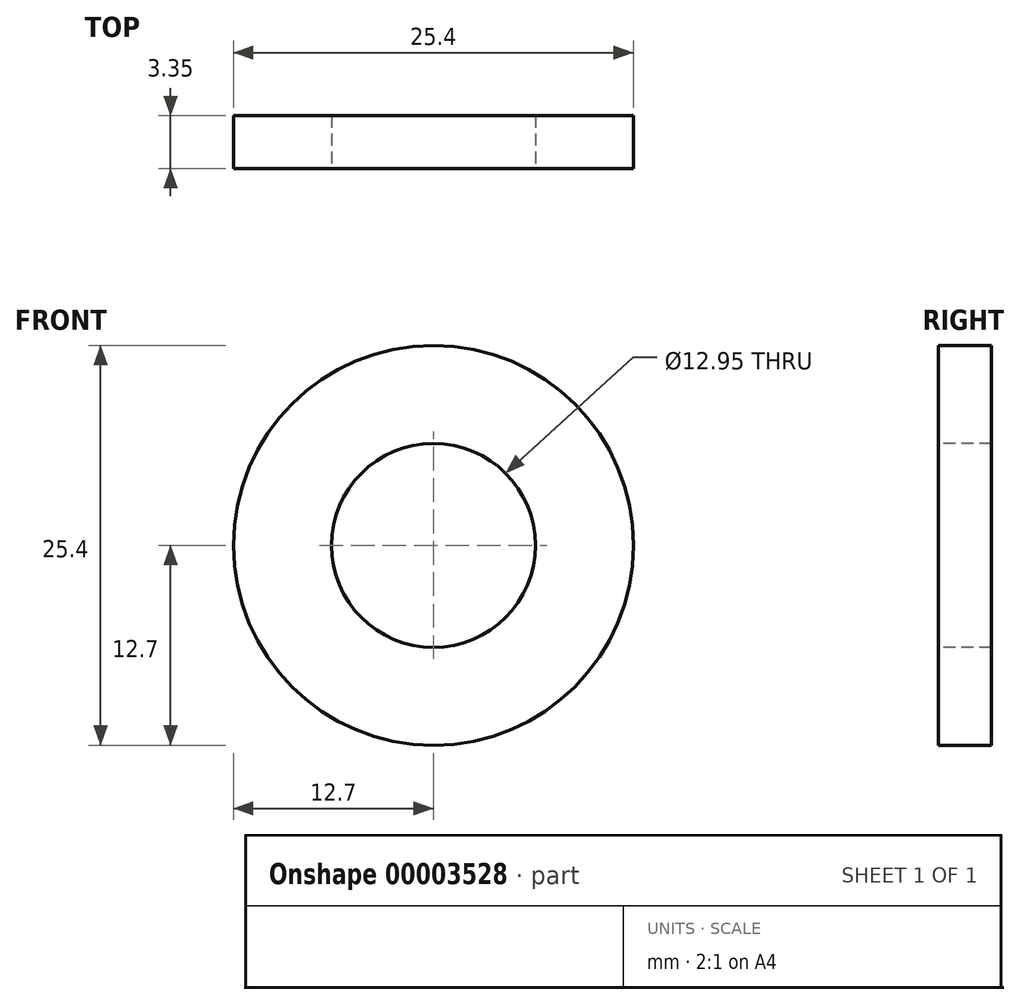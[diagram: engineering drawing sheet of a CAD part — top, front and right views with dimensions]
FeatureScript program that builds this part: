
annotation { "Feature Type Name" : "Feature", "Feature Type Description" : "" }
export const myFeature = defineFeature(function(context is Context, id is Id, definition is map)
    precondition{}
    {
        {
            var Q0;
            Q0=qCreatedBy(makeId("Right.planeOp"),FACE);
            var sketch = newSketch(context, id + "F0", { "sketchPlane" : qUnion([Q0])});
            skLineSegment(sketch, "E0.bottom", {"start": v(0, 6.47) * mm, "end": v(3.35, 6.47) * mm});
            skLineSegment(sketch, "E0.top", {"start": v(0, 12.7) * mm, "end": v(3.35, 12.7) * mm});
            skLineSegment(sketch, "E0.left", {"start": v(0, 6.47) * mm, "end": v(0, 12.7) * mm});
            skLineSegment(sketch, "E0.right", {"start": v(3.35, 6.47) * mm, "end": v(3.35, 12.7) * mm});
            skLineSegment(sketch, "E1", {"start": v(0, 0) * mm, "end": v(3.35, 0) * mm});
            skSolve(sketch);
        }
        {
            var Q0;
            Q0=makeQuery(id+"F0.imprint","IMPRINT",FACE,{"disambiguationData":[TD([[makeQuery(id+"F0.imprint","IMPRINT",EDGE,{"derivedFrom":sQuery(id+"F0.wireOp",EDGE,"E0.bottom")}),1.0]])]});
            var Q1;
            Q1=sQuery(id+"F0.wireOp",EDGE,"E1");
            revolve(context, id + "F1", {"entities" : qUnion([Q0]), "axis" : qUnion([Q1]), "revolveType" : RevolveType.FULL});
        }
    });
